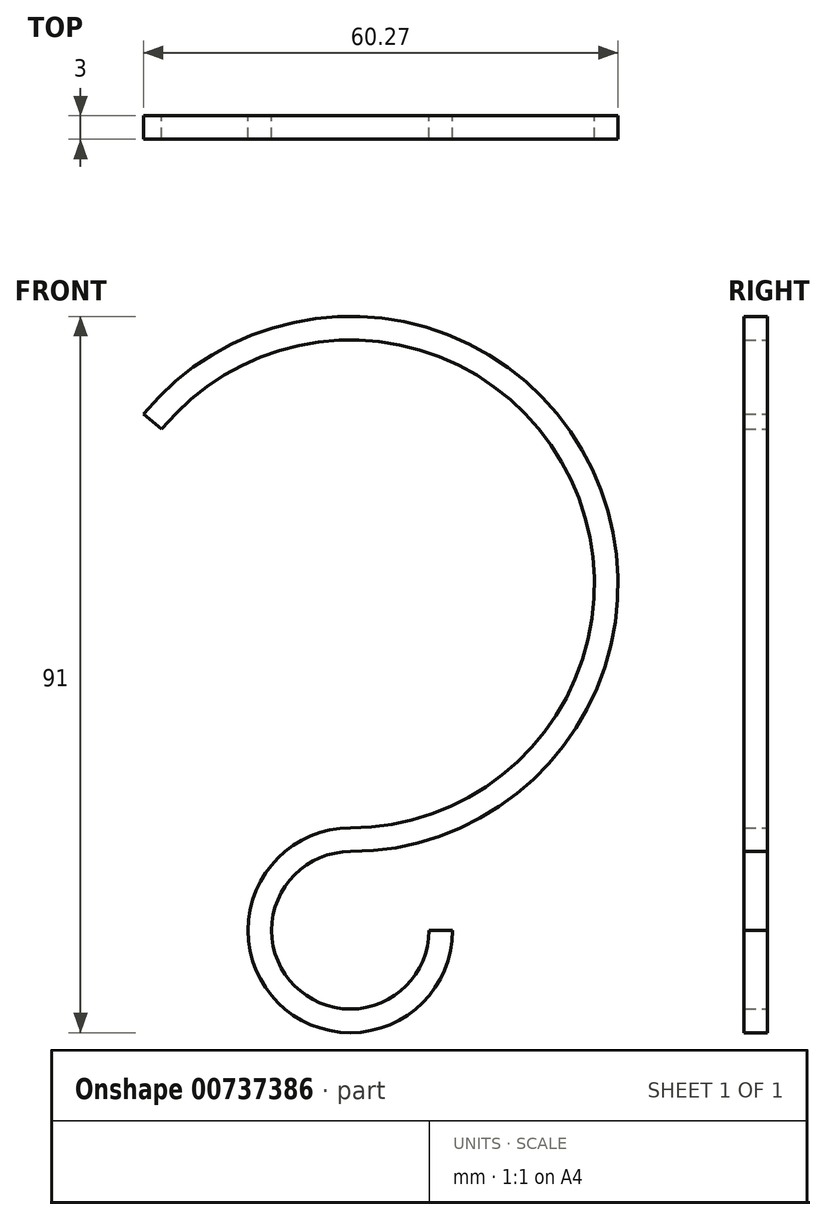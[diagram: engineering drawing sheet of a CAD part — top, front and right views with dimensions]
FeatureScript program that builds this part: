
annotation { "Feature Type Name" : "Feature", "Feature Type Description" : "" }
export const myFeature = defineFeature(function(context is Context, id is Id, definition is map)
    precondition{}
    {
        {
            var Q0;
            Q0=qCreatedBy(makeId("Front.planeOp"),FACE);
            var sketch = newSketch(context, id + "F0", { "sketchPlane" : qUnion([Q0])});
            skCircle(sketch, "E0", {"center": v(0, 0) * mm, "radius": 31 * mm});
            skCircle(sketch, "E1", {"center": v(0, 0) * mm, "radius": 34 * mm});
            skCircle(sketch, "E2", {"center": v(0, -44) * mm, "radius": 13 * mm});
            skCircle(sketch, "E3", {"center": v(0, -44) * mm, "radius": 10 * mm});
            skLineSegment(sketch, "E4", {"start": v(-7.26, -33.22) * mm, "end": v(0, 0) * mm});
            skLineSegment(sketch, "E5", {"start": v(0, 0) * mm, "end": v(-26.27, 21.58) * mm});
            skLineSegment(sketch, "E6", {"start": v(-26.27, 21.58) * mm, "end": v(-7.26, -33.22) * mm});
            skLineSegment(sketch, "E7", {"start": v(0, -44) * mm, "end": v(21.3, -44) * mm});
            skSolve(sketch);
        }
        {
            var Q0;
            {var subQ0=sQuery(id+"F0.wireOp",EDGE,"E5");var subQ1=sQuery(id+"F0.wireOp",EDGE,"E0");var subQ2=makeQuery(id+"F0.imprint","INTERSECT",VERTEX,{"derivedFrom":[subQ1,subQ0]});Q0=makeQuery(id+"F0.imprint","IMPRINT",FACE,{"disambiguationData":[TD([[makeQuery(id+"F0.imprint","IMPRINT",EDGE,{"disambiguationData":[TD([[subQ2,1.0]])],"derivedFrom":subQ1}),-1.0]])]});}
            var Q1;
            {var subQ0=sQuery(id+"F0.wireOp",EDGE,"E2");var subQ1=sQuery(id+"F0.wireOp",EDGE,"E1");var subQ5=makeQuery(id+"F0.imprint","INTERSECT",VERTEX,{"derivedFrom":[subQ1,subQ0]});Q1=makeQuery(id+"F0.imprint","IMPRINT",FACE,{"disambiguationData":[TD([[makeQuery(id+"F0.imprint","IMPRINT",EDGE,{"disambiguationData":[TD([[subQ5,1.0]])],"derivedFrom":subQ1}),1.0]])]});}
            var Q2;
            {var subQ3=sQuery(id+"F0.wireOp",EDGE,"E3");var subQ5=sQuery(id+"F0.wireOp",EDGE,"E7");var subQ7=makeQuery(id+"F0.imprint","INTERSECT",VERTEX,{"derivedFrom":[subQ3,subQ5]});Q2=makeQuery(id+"F0.imprint","IMPRINT",FACE,{"disambiguationData":[TD([[makeQuery(id+"F0.imprint","IMPRINT",EDGE,{"disambiguationData":[TD([[subQ7,1.0]])],"derivedFrom":subQ3}),-1.0]])]});}
            extrude(context, id + "F1", {"entities" : qUnion([Q0, Q1, Q2]), "depth" : 3 * mm, "offsetDistance" : 25 * mm});
        }
    });
